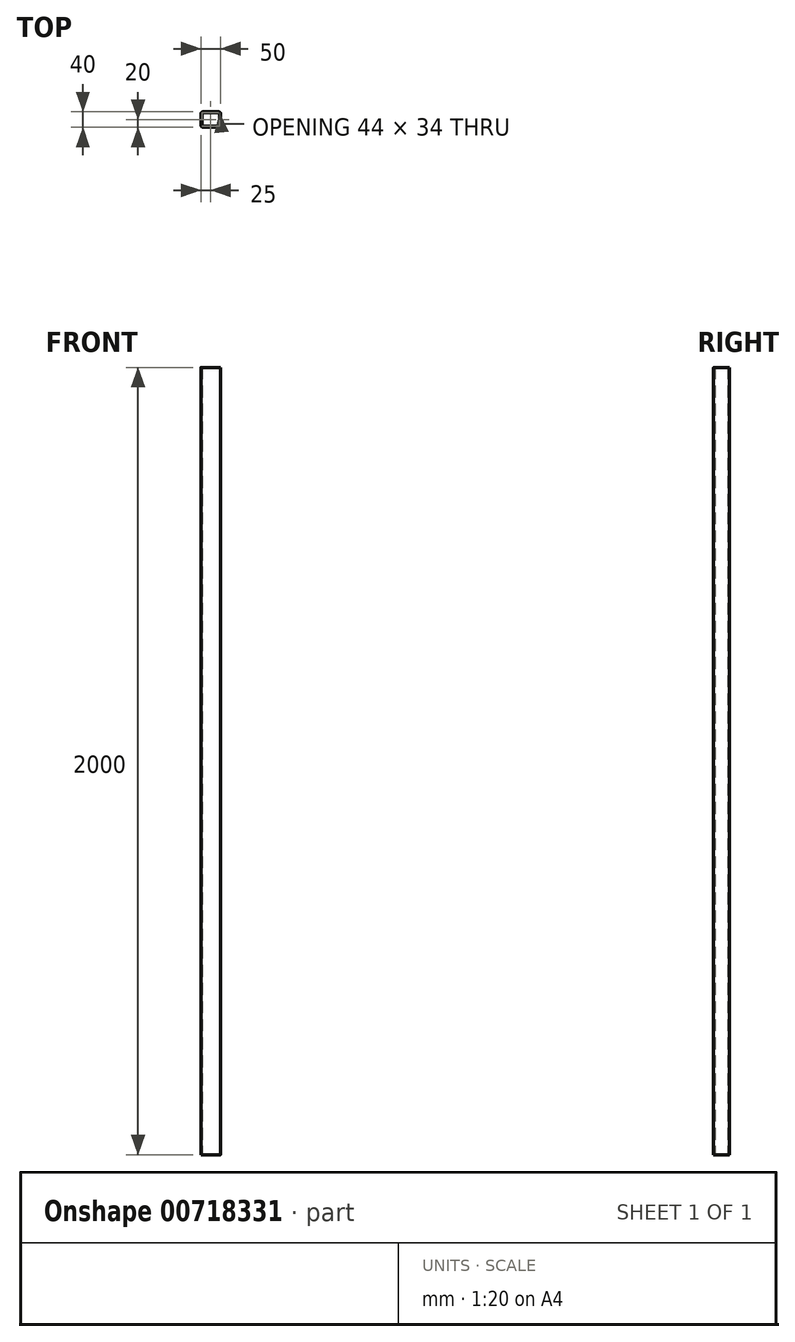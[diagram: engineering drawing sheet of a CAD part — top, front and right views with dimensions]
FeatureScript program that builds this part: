
annotation { "Feature Type Name" : "Feature", "Feature Type Description" : "" }
export const myFeature = defineFeature(function(context is Context, id is Id, definition is map)
    precondition{}
    {
        {
            var Q0;
            Q0=qCreatedBy(makeId("Top.planeOp"),FACE);
            var sketch = newSketch(context, id + "F0", { "sketchPlane" : qUnion([Q0])});
            skLineSegment(sketch, "E0.bottom", {"start": v(19, 20) * mm, "end": v(-19, 20) * mm});
            skLineSegment(sketch, "E0.top", {"start": v(19, -20) * mm, "end": v(-19, -20) * mm});
            skLineSegment(sketch, "E0.left", {"start": v(25, 14) * mm, "end": v(25, -14) * mm});
            skLineSegment(sketch, "E0.right", {"start": v(-25, 14) * mm, "end": v(-25, -14) * mm});
            skPoint(sketch, "E0.middle", {"position": v(0, 0) * mm});
            skPoint(sketch, "E1.visualSharp", {"position": v(-25, 20) * mm});
            skArc(sketch, "E1.filletArc", {"start": v(-19, 20) * mm, "mid": v(-23.24, 18.24) * mm, "end": v(-25, 14) * mm});
            skPoint(sketch, "E2.visualSharp", {"position": v(25, 20) * mm});
            skArc(sketch, "E2.filletArc", {"start": v(25, 14) * mm, "mid": v(23.24, 18.24) * mm, "end": v(19, 20) * mm});
            skPoint(sketch, "E3.visualSharp", {"position": v(25, -20) * mm});
            skArc(sketch, "E3.filletArc", {"start": v(19, -20) * mm, "mid": v(23.24, -18.24) * mm, "end": v(25, -14) * mm});
            skPoint(sketch, "E4.visualSharp", {"position": v(-25, -20) * mm});
            skArc(sketch, "E4.filletArc", {"start": v(-25, -14) * mm, "mid": v(-23.24, -18.24) * mm, "end": v(-19, -20) * mm});
            skLineSegment(sketch, "E5.0", {"start": v(-22, 14) * mm, "end": v(-22, -14) * mm});
            skLineSegment(sketch, "E5.1", {"start": v(19, 17) * mm, "end": v(-19, 17) * mm});
            skLineSegment(sketch, "E5.2", {"start": v(22, 14) * mm, "end": v(22, -14) * mm});
            skLineSegment(sketch, "E5.3", {"start": v(19, -17) * mm, "end": v(-19, -17) * mm});
            skPoint(sketch, "E6.visualSharp", {"position": v(-22, -17) * mm});
            skArc(sketch, "E6.filletArc", {"start": v(-22, -14) * mm, "mid": v(-21.12, -16.12) * mm, "end": v(-19, -17) * mm});
            skPoint(sketch, "E7.visualSharp", {"position": v(22, -17) * mm});
            skArc(sketch, "E7.filletArc", {"start": v(19, -17) * mm, "mid": v(21.12, -16.12) * mm, "end": v(22, -14) * mm});
            skPoint(sketch, "E8.visualSharp", {"position": v(22, 17) * mm});
            skArc(sketch, "E8.filletArc", {"start": v(22, 14) * mm, "mid": v(21.12, 16.12) * mm, "end": v(19, 17) * mm});
            skPoint(sketch, "E9.visualSharp", {"position": v(-22, 17) * mm});
            skArc(sketch, "E9.filletArc", {"start": v(-19, 17) * mm, "mid": v(-21.12, 16.12) * mm, "end": v(-22, 14) * mm});
            skSolve(sketch);
        }
        {
            var Q0;
            Q0=makeQuery(id+"F0.imprint","IMPRINT",FACE,{"disambiguationData":[TD([[makeQuery(id+"F0.imprint","IMPRINT",EDGE,{"derivedFrom":sQuery(id+"F0.wireOp",EDGE,"E0.bottom")}),1.0]])]});
            extrude(context, id + "F1", {"entities" : qUnion([Q0]), "depth" : 2000 * mm, "offsetDistance" : 25 * mm});
        }
    });
